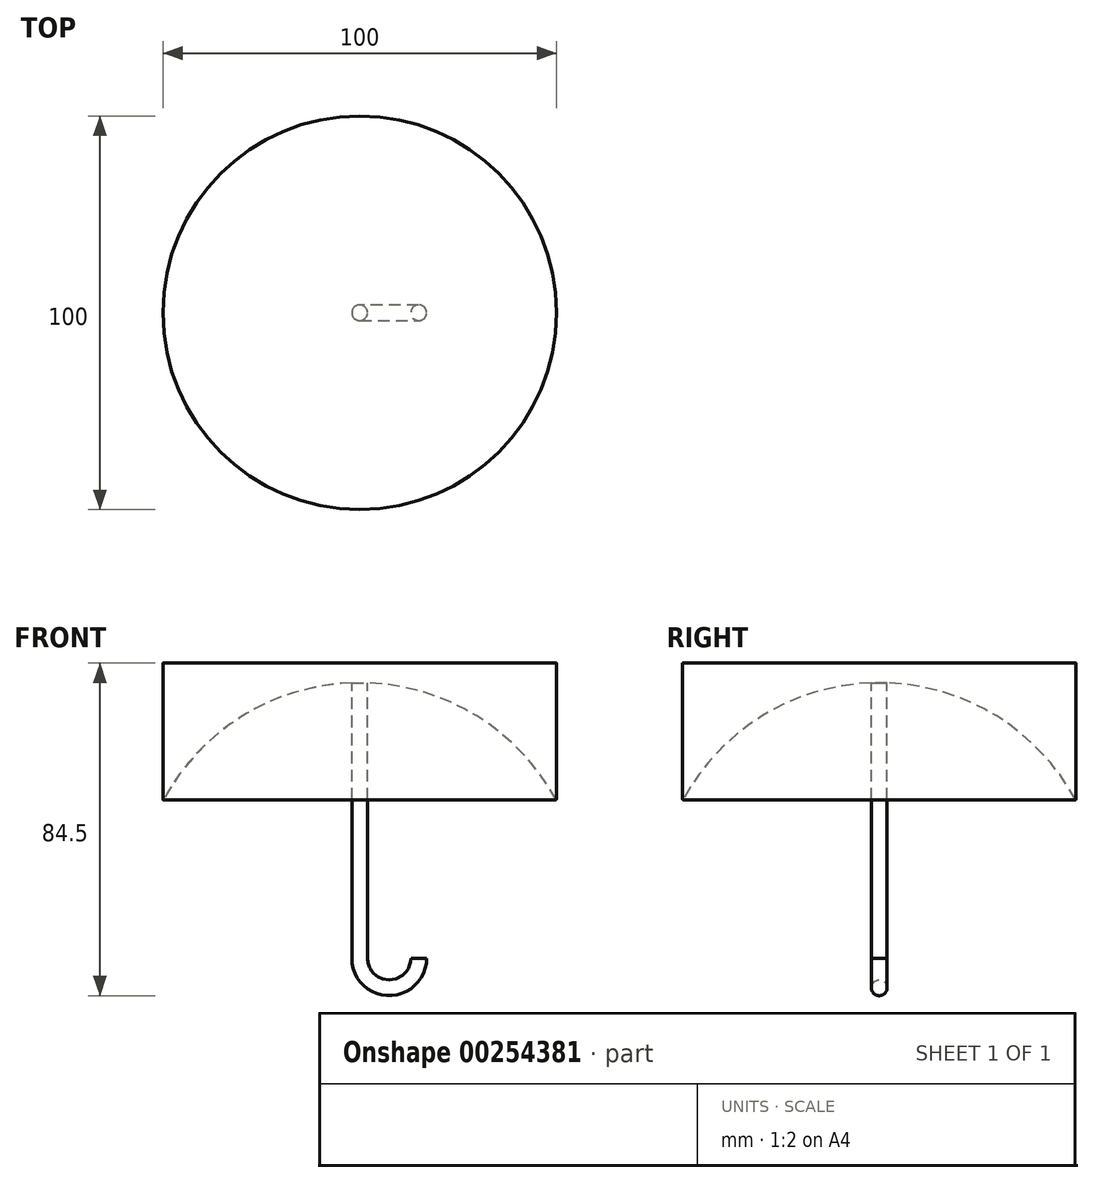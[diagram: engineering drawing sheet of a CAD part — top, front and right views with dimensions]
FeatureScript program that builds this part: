
annotation { "Feature Type Name" : "Feature", "Feature Type Description" : "" }
export const myFeature = defineFeature(function(context is Context, id is Id, definition is map)
    precondition{}
    {
        {
            var Q0;
            Q0=qCreatedBy(makeId("Front.planeOp"),FACE);
            var sketch = newSketch(context, id + "F0", { "sketchPlane" : qUnion([Q0])});
            skArc(sketch, "E0", {"start": v(0, 0) * mm, "mid": v(7.5, -7.5) * mm, "end": v(15, 0) * mm});
            skLineSegment(sketch, "E1", {"start": v(0, 0) * mm, "end": v(15, 0) * mm, "construction": true});
            skLineSegment(sketch, "E2", {"start": v(0, 0) * mm, "end": v(0, 75) * mm});
            skSolve(sketch);
        }
        {
            var Q0;
            Q0=qCreatedBy(makeId("Top.planeOp"),FACE);
            var sketch = newSketch(context, id + "F1", { "sketchPlane" : qUnion([Q0])});
            skCircle(sketch, "E3", {"center": v(15, 0) * mm, "radius": 2 * mm});
            skSolve(sketch);
        }
        {
            var Q0;
            Q0=makeQuery(id+"F1.imprint","IMPRINT",FACE,{"disambiguationData":[TD([[makeQuery(id+"F1.imprint","IMPRINT",EDGE,{"derivedFrom":sQuery(id+"F1.wireOp",EDGE,"E3")}),1.0]])]});
            var Q1;
            Q1=sQuery(id+"F0.wireOp",EDGE,"E2");
            var Q2;
            Q2=sQuery(id+"F0.wireOp",EDGE,"E0");
            sweep(context, id + "F2", {"profiles" : qUnion([Q0]), "path" : qUnion([Q1, Q2])});
        }
        {
            var Q0;
            Q0=qCreatedBy(makeId("Front.planeOp"),FACE);
            var sketch = newSketch(context, id + "F3", { "sketchPlane" : qUnion([Q0])});
            skArc(sketch, "E4", {"start": v(-50, 40) * mm, "mid": v(0, 70) * mm, "end": v(50, 40) * mm});
            skLineSegment(sketch, "E5", {"start": v(-50, 40) * mm, "end": v(50, 40) * mm, "construction": true});
            skLineSegment(sketch, "E6", {"start": v(0, 13.33) * mm, "end": v(0, 70) * mm});
            skLineSegment(sketch, "E7", {"start": v(-50, 40) * mm, "end": v(-50, 75) * mm});
            skLineSegment(sketch, "E8", {"start": v(-50, 75) * mm, "end": v(50, 75) * mm});
            skLineSegment(sketch, "E9", {"start": v(50, 75) * mm, "end": v(50, 40) * mm});
            skLineSegment(sketch, "E10", {"start": v(0, 70) * mm, "end": v(0, 75) * mm});
            skSolve(sketch);
        }
        {
            var Q0;
            {var subQ0=sQuery(id+"F3.wireOp",EDGE,"E7");Q0=makeQuery(id+"F3.imprint","IMPRINT",FACE,{"disambiguationData":[TD([[makeQuery(id+"F3.imprint","IMPRINT",EDGE,{"derivedFrom":subQ0}),-1.0]])]});}
            var Q1;
            Q1=sQuery(id+"F3.wireOp",EDGE,"E10");
            revolve(context, id + "F4", {"operationType" : NewBodyOperationType.ADD, "entities" : qUnion([Q0]), "axis" : qUnion([Q1]), "revolveType" : RevolveType.FULL});
        }
        {
            var Q0;
            Q0=makeQuery(id+"F4.opRevolve","SWEPT_EDGE",EDGE,{"disambiguationData":[OSD([sQuery(id+"F3.wireOp",EDGE,"E7"),sQuery(id+"F3.wireOp",EDGE,"E8")])]});
            var Q1;
            Q1=makeQuery(id+"F4.opRevolve","SWEPT_EDGE",EDGE,{"disambiguationData":[OSD([sQuery(id+"F3.wireOp",EDGE,"E4"),sQuery(id+"F3.wireOp",EDGE,"E7")])]});
            fillet(context, id + "F5", {"entities" : qUnion([Q0, Q1]), "radius" : .1 * mm, "tangentPropagation" : true, "allowEdgeOverflow" : false});
        }
    });
